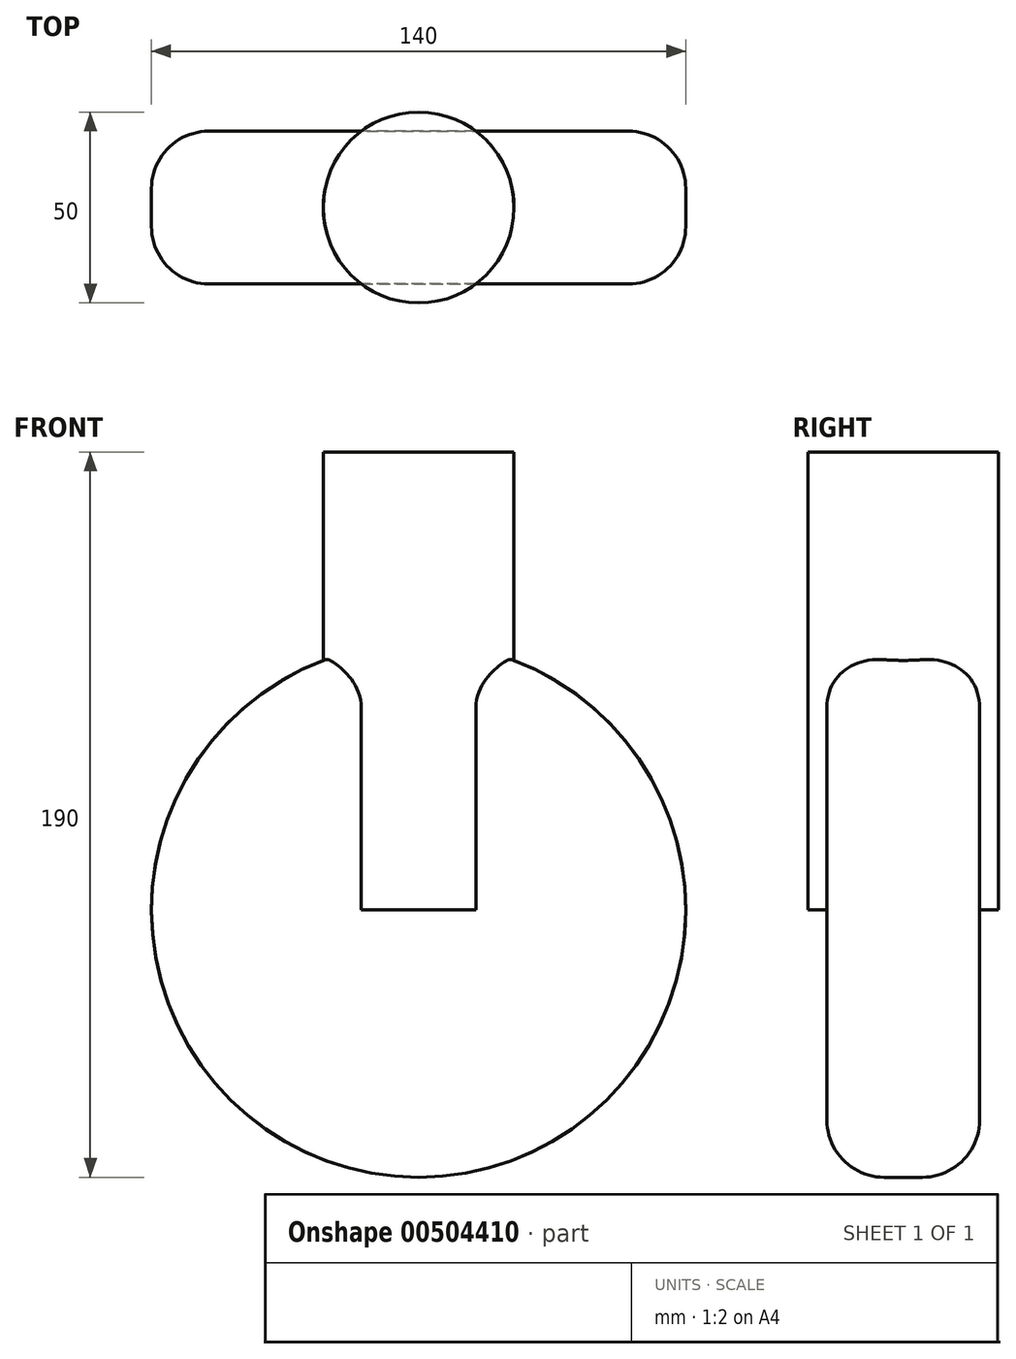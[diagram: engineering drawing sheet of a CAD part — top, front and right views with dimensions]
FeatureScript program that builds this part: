
annotation { "Feature Type Name" : "Feature", "Feature Type Description" : "" }
export const myFeature = defineFeature(function(context is Context, id is Id, definition is map)
    precondition{}
    {
        {
            var Q0;
            Q0=qCreatedBy(makeId("Front.planeOp"),FACE);
            var sketch = newSketch(context, id + "F0", { "sketchPlane" : qUnion([Q0])});
            skCircle(sketch, "E0", {"center": v(0, 0) * mm, "radius": 70 * mm});
            skSolve(sketch);
        }
        {
            var Q0;
            Q0=makeQuery(id+"F0.imprint","IMPRINT",FACE,{"disambiguationData":[TD([[makeQuery(id+"F0.imprint","IMPRINT",EDGE,{"derivedFrom":sQuery(id+"F0.wireOp",EDGE,"E0")}),1.0]])]});
            extrude(context, id + "F1", {"entities" : qUnion([Q0]), "depth" : 40 * mm, "offsetDistance" : 25 * mm, "symmetric" : true});
        }
        {
            var Q0;
            Q0=makeQuery(id+"F1.opExtrude","CAP_EDGE",EDGE,{"disambiguationData":[OSD([sQuery(id+"F0.wireOp",EDGE,"E0")])],"isStart":false});
            var Q1;
            Q1=makeQuery(id+"F1.opExtrude","CAP_EDGE",EDGE,{"disambiguationData":[OSD([sQuery(id+"F0.wireOp",EDGE,"E0")])],"isStart":true});
            fillet(context, id + "F2", {"entities" : qUnion([Q0, Q1]), "radius" : 15 * mm, "tangentPropagation" : true, "allowEdgeOverflow" : false});
        }
        {
            var Q0;
            Q0=qCreatedBy(makeId("Front.planeOp"),FACE);
            var sketch = newSketch(context, id + "F3", { "sketchPlane" : qUnion([Q0])});
            skLineSegment(sketch, "E1", {"start": v(-25, 0) * mm, "end": v(-25, 120) * mm});
            skLineSegment(sketch, "E2", {"start": v(-25, 0) * mm, "end": v(0, 0) * mm});
            skLineSegment(sketch, "E3", {"start": v(0, 0) * mm, "end": v(0, 120) * mm});
            skLineSegment(sketch, "E4", {"start": v(0, 120) * mm, "end": v(-25, 120) * mm});
            skSolve(sketch);
        }
        {
            var Q0;
            Q0=makeQuery(id+"F3.imprint","IMPRINT",FACE,{"disambiguationData":[TD([[makeQuery(id+"F3.imprint","IMPRINT",EDGE,{"derivedFrom":sQuery(id+"F3.wireOp",EDGE,"E1")}),-1.0]])]});
            var Q1;
            Q1=sQuery(id+"F3.wireOp",EDGE,"E3");
            revolve(context, id + "F4", {"operationType" : NewBodyOperationType.ADD, "entities" : qUnion([Q0]), "axis" : qUnion([Q1]), "revolveType" : RevolveType.FULL});
        }
    });
